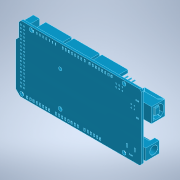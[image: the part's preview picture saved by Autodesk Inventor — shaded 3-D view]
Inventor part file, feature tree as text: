
AUTODESK INVENTOR PART (.ipt)
format: ipt  version: 2021 (Build 250183000, 183)  size: 1,230,848 bytes
history: native  units: in
note: dims shown in document units (in); Inventor stores cm internally (conversion verified against a paired STEP export)
features: fillet x1
ambient origin geometry x8: Origin, YZ Plane, XZ Plane, XY Plane, X Axis, Y Axis, Z Axis, Center Point
bodies: Solid1 (feature_tree)
feature tree (1):
  fillet  "Fillet5"  [1 undecoded]
note: 1 required parameter value undecoded (feature->parameter linkage not recoverable at this tier; creation-order binding heuristic only, values carry confidence <= 0.55)
